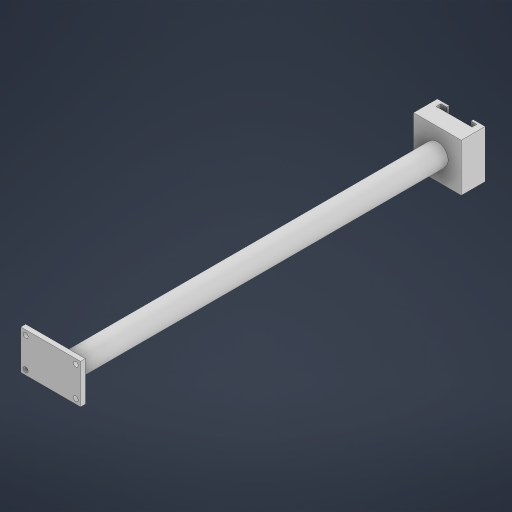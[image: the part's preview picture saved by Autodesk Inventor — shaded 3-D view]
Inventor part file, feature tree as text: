
AUTODESK INVENTOR PART (.ipt)
format: ipt  version: 2024 (Build 280153000, 153)  size: 251,392 bytes
history: native  units: mm
features: extrude x5, sketch x4, other x1
ambient origin geometry x8: Origin, YZ Plane, XZ Plane, XY Plane, X Axis, Y Axis, Z Axis, Center Point
bodies: Body1 (feature_tree)
feature tree (10):
  other  "솔리드1"
  sketch  "스케치1"
  extrude  "돌출1"  Depth=25.0mm
  extrude  "돌출2"  Depth=16.5mm
  extrude  "돌출3"  Depth=2.0mm
  extrude  "돌출4"  Depth=2.0mm
  extrude  "돌출5"  Depth=2.0mm
  sketch  "스케치2"
  sketch  "스케치3"
  sketch  "스케치4"
